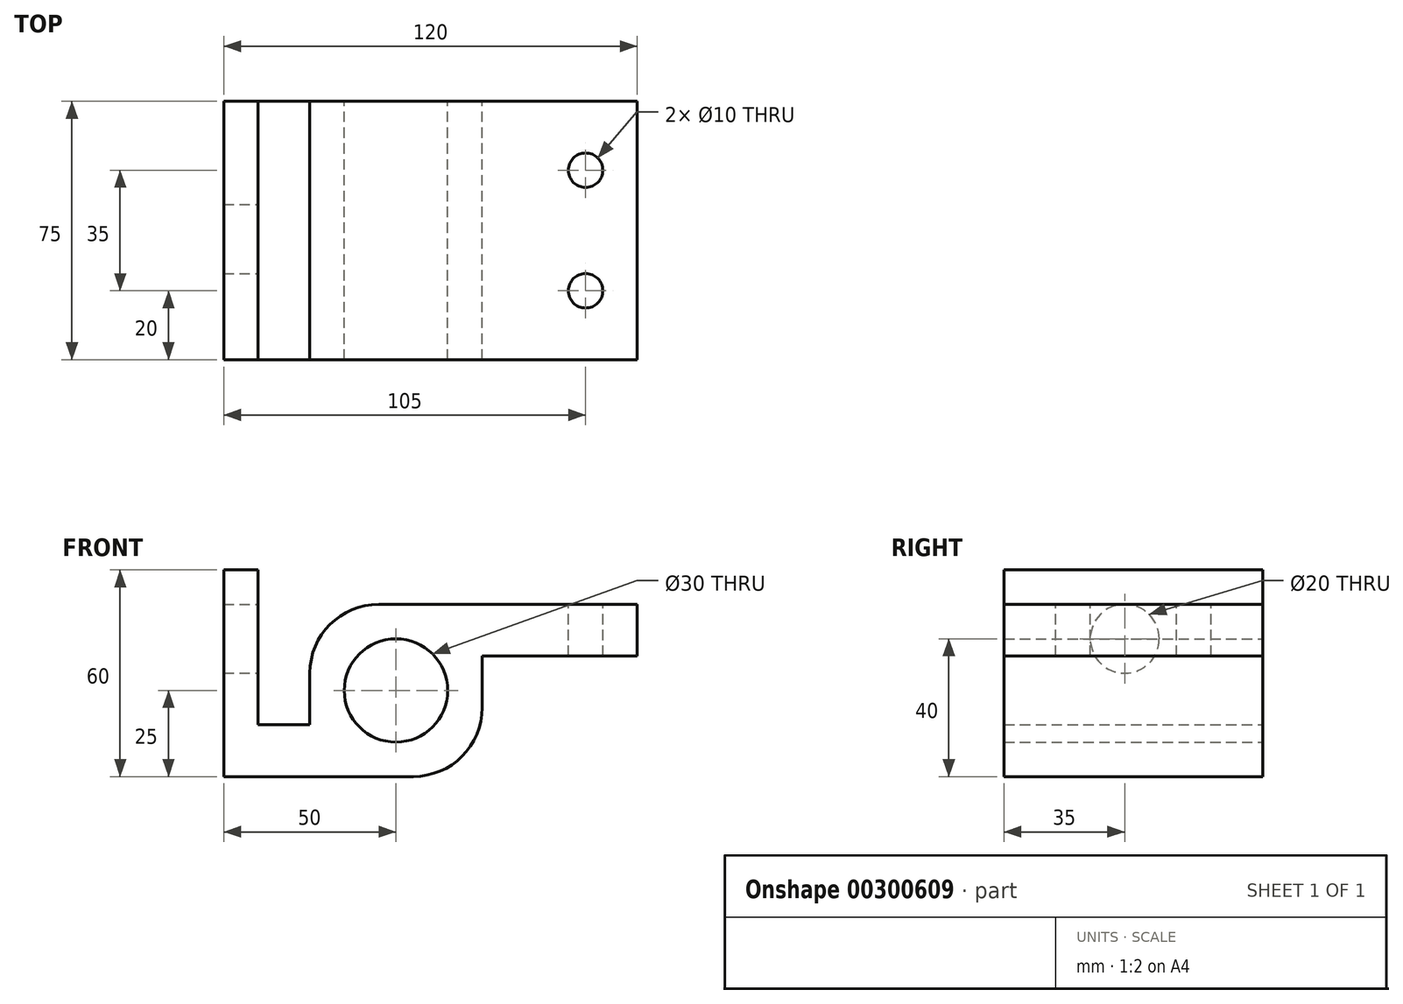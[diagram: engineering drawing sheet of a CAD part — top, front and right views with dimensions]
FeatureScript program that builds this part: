
annotation { "Feature Type Name" : "Feature", "Feature Type Description" : "" }
export const myFeature = defineFeature(function(context is Context, id is Id, definition is map)
    precondition{}
    {
        {
            var Q0;
            Q0=qCreatedBy(makeId("Front.planeOp"),FACE);
            var sketch = newSketch(context, id + "F0", { "sketchPlane" : qUnion([Q0])});
            skLineSegment(sketch, "E0.bottom", {"start": v(60, 37.5) * mm, "end": v(-60, 37.5) * mm});
            skLineSegment(sketch, "E0.top", {"start": v(60, -37.5) * mm, "end": v(-60, -37.5) * mm});
            skLineSegment(sketch, "E0.left", {"start": v(60, 37.5) * mm, "end": v(60, -37.5) * mm});
            skLineSegment(sketch, "E0.right", {"start": v(-60, 37.5) * mm, "end": v(-60, -37.5) * mm});
            skPoint(sketch, "E0.middle", {"position": v(0, 0) * mm});
            skCircle(sketch, "E1", {"center": v(-10, -12.5) * mm, "radius": 15 * mm});
            skLineSegment(sketch, "E2.bottom", {"start": v(-60, 37.5) * mm, "end": v(-50, 37.5) * mm});
            skLineSegment(sketch, "E2.top", {"start": v(-60, 22.5) * mm, "end": v(-50, 22.5) * mm});
            skLineSegment(sketch, "E2.left", {"start": v(-60, 37.5) * mm, "end": v(-60, 22.5) * mm});
            skLineSegment(sketch, "E2.right", {"start": v(-50, 37.5) * mm, "end": v(-50, 22.5) * mm});
            skLineSegment(sketch, "E3.top", {"start": v(-60, -37.5) * mm, "end": v(-50, -37.5) * mm});
            skLineSegment(sketch, "E3.left", {"start": v(-60, 22.5) * mm, "end": v(-60, -37.5) * mm});
            skLineSegment(sketch, "E3.right", {"start": v(-50, 22.5) * mm, "end": v(-50, -37.5) * mm});
            skLineSegment(sketch, "E4", {"start": v(-50, -22.5) * mm, "end": v(-35, -22.5) * mm});
            skLineSegment(sketch, "E5", {"start": v(-35, -22.5) * mm, "end": v(-35, -7.5) * mm});
            skLineSegment(sketch, "E6", {"start": v(-15, 12.5) * mm, "end": v(60, 12.5) * mm});
            skLineSegment(sketch, "E7", {"start": v(-60, -37.5) * mm, "end": v(-5, -37.5) * mm});
            skLineSegment(sketch, "E8", {"start": v(15, -17.5) * mm, "end": v(15, -2.5) * mm});
            skLineSegment(sketch, "E9", {"start": v(15, -2.5) * mm, "end": v(60, -2.5) * mm});
            skPoint(sketch, "E10.visualSharp", {"position": v(-35, 12.5) * mm});
            skArc(sketch, "E10.filletArc", {"start": v(-15, 12.5) * mm, "mid": v(-29.14, 6.64) * mm, "end": v(-35, -7.5) * mm});
            skPoint(sketch, "E11.visualSharp", {"position": v(15, -37.5) * mm});
            skArc(sketch, "E11.filletArc", {"start": v(-5, -37.5) * mm, "mid": v(9.14, -31.64) * mm, "end": v(15, -17.5) * mm});
            skSolve(sketch);
        }
        {
            var Q0;
            Q0=makeQuery(id+"F0.imprint","IMPRINT",FACE,{"disambiguationData":[TD([[makeQuery(id+"F0.imprint","IMPRINT",EDGE,{"derivedFrom":sQuery(id+"F0.wireOp",EDGE,"E1")}),-1.0]])]});
            var Q1;
            {var subQ4=sQuery(id+"F0.wireOp",EDGE,"E2.top");Q1=makeQuery(id+"F0.imprint","IMPRINT",FACE,{"disambiguationData":[TD([[makeQuery(id+"F0.imprint","IMPRINT",EDGE,{"derivedFrom":subQ4}),-1.0]])]});}
            var Q2;
            Q2=makeQuery(id+"F0.imprint","IMPRINT",FACE,{"disambiguationData":[TD([[makeQuery(id+"F0.imprint","IMPRINT",EDGE,{"derivedFrom":sQuery(id+"F0.wireOp",EDGE,"E2.bottom")}),-1.0]])]});
            extrude(context, id + "F1", {"entities" : qUnion([Q0, Q1, Q2]), "depth" : 75 * mm});
        }
        {
            var Q0;
            Q0=makeQuery(id+"F1.opExtrude","SWEPT_FACE",FACE,{"disambiguationData":[OSD([sQuery(id+"F0.wireOp",EDGE,"E6")])]});
            var sketch = newSketch(context, id + "F2", { "sketchPlane" : qUnion([Q0])});
            skCircle(sketch, "E12", {"center": v(45, -20) * mm, "radius": 5 * mm});
            skCircle(sketch, "E13", {"center": v(45, -55) * mm, "radius": 5 * mm});
            skSolve(sketch);
        }
        {
            var Q0;
            Q0 = qSketchRegion(id + "F2", true);
            extrude(context, id + "F3", {"entities" : qUnion([Q0]), "operationType" : NewBodyOperationType.REMOVE, "endBound" : BoundingType.THROUGH_ALL, "oppositeDirection" : true, "depth" : 25 * mm});
        }
        {
            var Q0;
            Q0=makeQuery(id+"F1.opExtrude","SWEPT_FACE",FACE,{"disambiguationData":[OSD([sQuery(id+"F0.wireOp",EDGE,"E2.right"),sQuery(id+"F0.wireOp",EDGE,"E3.right")])]});
            var sketch = newSketch(context, id + "F4", { "sketchPlane" : qUnion([Q0])});
            skCircle(sketch, "E14", {"center": v(-40, 2.5) * mm, "radius": 10 * mm});
            skLineSegment(sketch, "E15", {"start": v(-75, 22.5) * mm, "end": v(-60, 37.5) * mm});
            skLineSegment(sketch, "E16", {"start": v(-15, 37.5) * mm, "end": v(0, 22.5) * mm});
            skSolve(sketch);
        }
        {
            var Q0;
            Q0=makeQuery(id+"F4.imprint","IMPRINT",FACE,{"disambiguationData":[TD([[makeQuery(id+"F4.imprint","IMPRINT",EDGE,{"derivedFrom":sQuery(id+"F4.wireOp",EDGE,"E14")}),1.0]])]});
            var Q1;
            {var subQ0=sQuery(id+"F4.wireOp",EDGE,"E15");Q1=makeQuery(id+"F4.imprint","IMPRINT",FACE,{"disambiguationData":[TD([[makeQuery(id+"F4.imprint","IMPRINT",EDGE,{"derivedFrom":subQ0}),1.0]])]});}
            var Q2;
            {var subQ0=sQuery(id+"F4.wireOp",EDGE,"E16");Q2=makeQuery(id+"F4.imprint","IMPRINT",FACE,{"disambiguationData":[TD([[makeQuery(id+"F4.imprint","IMPRINT",EDGE,{"derivedFrom":subQ0}),1.0]])]});}
            extrude(context, id + "F5", {"entities" : qUnion([Q0, Q1, Q2]), "operationType" : NewBodyOperationType.REMOVE, "endBound" : BoundingType.THROUGH_ALL, "oppositeDirection" : true, "depth" : 25 * mm});
        }
    });
